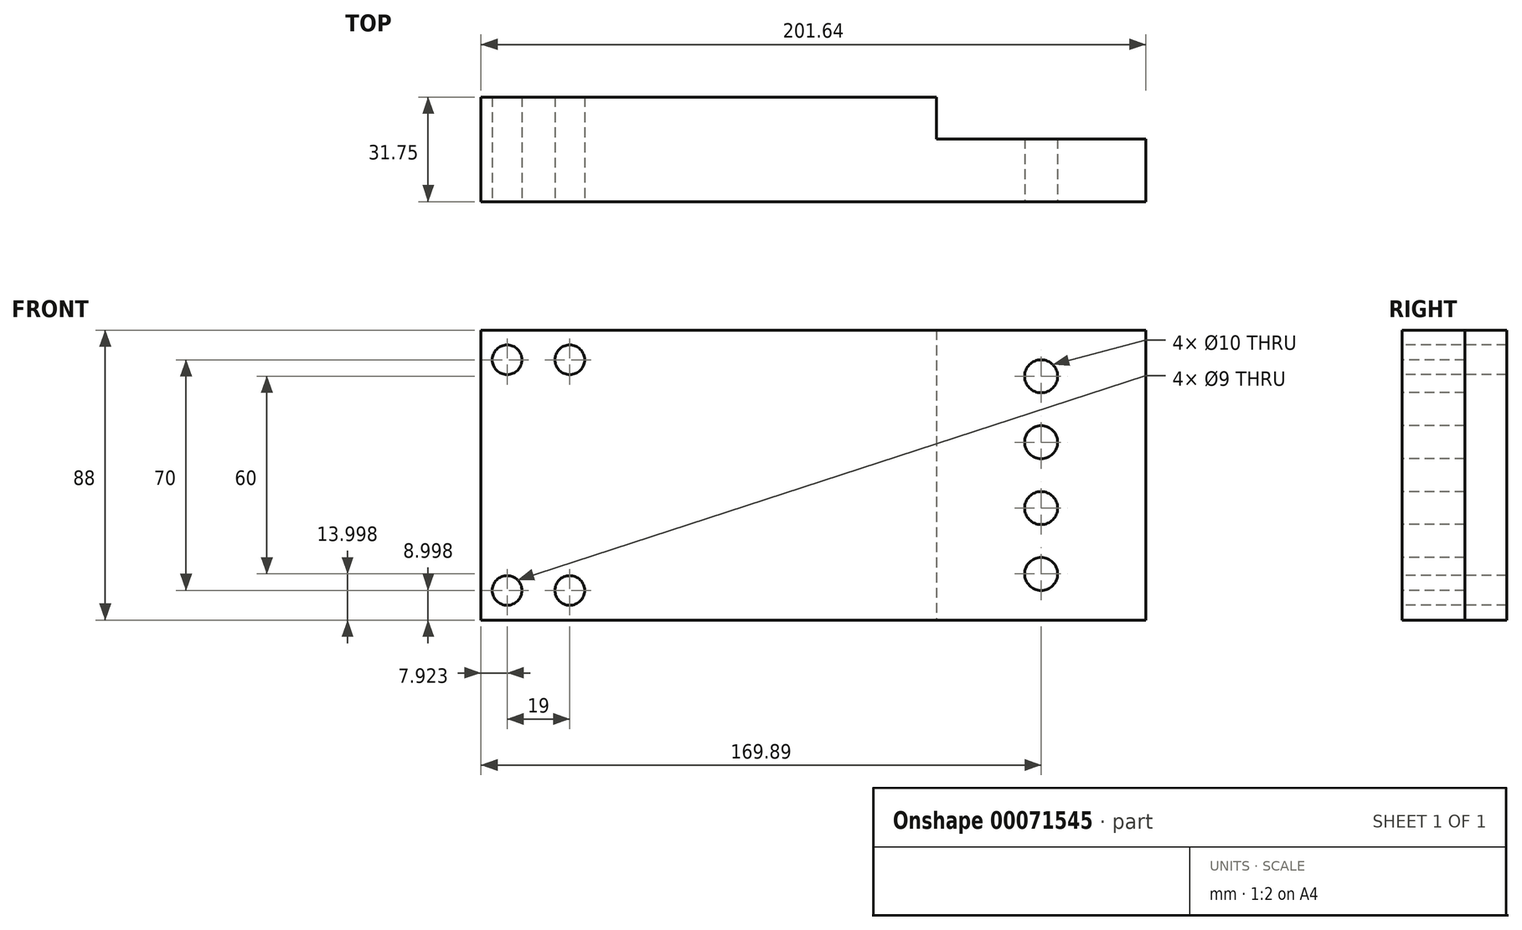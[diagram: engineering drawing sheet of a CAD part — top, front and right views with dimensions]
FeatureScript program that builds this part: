
annotation { "Feature Type Name" : "Feature", "Feature Type Description" : "" }
export const myFeature = defineFeature(function(context is Context, id is Id, definition is map)
    precondition{}
    {
        {
            var Q0;
            Q0=qCreatedBy(makeId("Front.planeOp"),FACE);
            var sketch = newSketch(context, id + "F0", { "sketchPlane" : qUnion([Q0])});
            skLineSegment(sketch, "E0.bottom", {"start": v(-104.3, 28.27) * mm, "end": v(97.34, 28.27) * mm});
            skLineSegment(sketch, "E0.top", {"start": v(-104.3, -59.73) * mm, "end": v(97.34, -59.73) * mm});
            skLineSegment(sketch, "E0.left", {"start": v(-104.3, 28.27) * mm, "end": v(-104.3, -59.73) * mm});
            skLineSegment(sketch, "E0.right", {"start": v(97.34, 28.27) * mm, "end": v(97.34, -59.73) * mm});
            skSolve(sketch);
        }
        {
            var Q0;
            Q0 = qSketchRegion(id + "F0", true);
            extrude(context, id + "F1", {"entities" : qUnion([Q0]), "depth" : 31.75 * mm});
        }
        {
            var Q0;
            Q0=makeQuery(id+"F1.opExtrude","SWEPT_FACE",FACE,{"disambiguationData":[OSD([sQuery(id+"F0.wireOp",EDGE,"E0.top")])]});
            var sketch = newSketch(context, id + "F2", { "sketchPlane" : qUnion([Q0])});
            skLineSegment(sketch, "E1.bottom", {"start": v(97.34, 0) * mm, "end": v(33.84, 0) * mm});
            skLineSegment(sketch, "E1.top", {"start": v(97.34, 12.7) * mm, "end": v(33.84, 12.7) * mm});
            skLineSegment(sketch, "E1.left", {"start": v(97.34, 0) * mm, "end": v(97.34, 12.7) * mm});
            skLineSegment(sketch, "E1.right", {"start": v(33.84, 0) * mm, "end": v(33.84, 12.7) * mm});
            skSolve(sketch);
        }
        {
            var Q0;
            Q0 = qSketchRegion(id + "F2", true);
            extrude(context, id + "F3", {"entities" : qUnion([Q0]), "operationType" : NewBodyOperationType.REMOVE, "endBound" : BoundingType.THROUGH_ALL, "oppositeDirection" : true, "depth" : 25 * mm});
        }
        {
            var Q0;
            Q0=makeQuery(id+"F1.opExtrude","CAP_FACE",FACE,{"disambiguationData":[OSD([sQuery(id+"F0.wireOp",EDGE,"E0.bottom"),sQuery(id+"F0.wireOp",EDGE,"E0.top"),sQuery(id+"F0.wireOp",EDGE,"E0.left"),sQuery(id+"F0.wireOp",EDGE,"E0.right")])],"isStart":false});
            var sketch = newSketch(context, id + "F4", { "sketchPlane" : qUnion([Q0])});
            skCircle(sketch, "E2", {"center": v(-96.38, -50.73) * mm, "radius": 4.5 * mm});
            skCircle(sketch, "E3.0.1.0", {"center": v(-96.38, 19.27) * mm, "radius": 4.5 * mm});
            skCircle(sketch, "E3.1.0.0", {"center": v(-77.38, -50.73) * mm, "radius": 4.5 * mm});
            skCircle(sketch, "E3.1.1.0", {"center": v(-77.38, 19.27) * mm, "radius": 4.5 * mm});
            skLineSegment(sketch, "E3.direction1", {"start": v(-96.38, -50.73) * mm, "end": v(-77.38, -50.73) * mm, "construction": true});
            skLineSegment(sketch, "E3.direction2", {"start": v(-96.38, -50.73) * mm, "end": v(-96.38, 19.27) * mm, "construction": true});
            skCircle(sketch, "E4", {"center": v(65.6, -45.73) * mm, "radius": 5 * mm});
            skCircle(sketch, "E5.0.1.0", {"center": v(65.6, -25.73) * mm, "radius": 5 * mm});
            skCircle(sketch, "E5.0.2.0", {"center": v(65.6, -5.73) * mm, "radius": 5 * mm});
            skCircle(sketch, "E5.0.3.0", {"center": v(65.6, 14.27) * mm, "radius": 5 * mm});
            skLineSegment(sketch, "E5.direction1", {"start": v(65.6, -45.73) * mm, "end": v(107.71, -45.73) * mm, "construction": true});
            skLineSegment(sketch, "E5.direction2", {"start": v(65.6, -45.73) * mm, "end": v(65.6, -25.73) * mm, "construction": true});
            skSolve(sketch);
        }
        {
            var Q0;
            Q0 = qSketchRegion(id + "F4", true);
            extrude(context, id + "F5", {"entities" : qUnion([Q0]), "operationType" : NewBodyOperationType.REMOVE, "endBound" : BoundingType.THROUGH_ALL, "oppositeDirection" : true, "depth" : 25 * mm});
        }
    });
